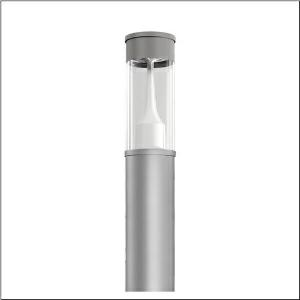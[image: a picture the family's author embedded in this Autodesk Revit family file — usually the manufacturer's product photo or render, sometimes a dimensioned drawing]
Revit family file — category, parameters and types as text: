
# Revit family: city-light_400_iq___st1_2a_5xa5305mf14hp_fa50
name_source: partatom
category: Lighting Fixtures
units: mm (PartAtom-declared; Revit-internal decimal feet)

## family parameters
Cut with Voids When Loaded = No
Host = Face
Light Source = No
Part Type = Normal
Room Calculation Point = No
Round Connector Dimension = Use Diameter
Shared = No

## types (1)
- --- (1 x LED, 4240 lm, 33.6 W, 2700K)
    Apparent Load = 34 VA
    CIE Flux Codes = 22 61 94 96 100
    Color Rendering = 70
    Color Temperature = 2700K
    Default Elevation = 1800 mm
    Description = City-Light 400 iQ, light pillar, Module 540 iQ-SR, primary light control with 3 zone facetted reflector, of plastic, silver coated, highly specular, structured, primary optical cover: cover, of PMMA, transparent, partly coated, light distribution: ST1.2a, primary light characteristic: asymmetric, LED, High Power LED, rated luminous flux: 4.240lm, luminous efficacy: 126lm/W, light colour: 727, colour temperature: 2700K, control gear: ECG iQ, control: presetting dimming logarithmic, Street-Remote, Auto-Match, Temp-Guard, Lumen-Switch, Night-Set, Smart-Wire, Light-Fading, Desk-Remote (wireless, voltage-free reading and setting of iQ features in the workshop via application-optimized NFC function/RFID function), optimised constant luminous flux control (CLO 2.0), with terminal, 6-pole, max. 2.5mm², mains connection: 230..240V, AC, 50/60Hz, start of lifetime: 34W, end of service life: 36W, reduction: 15W, luminaire housing, cylindrical, of extruded aluminium section, coated, Siteco® metallic grey (DB 702S), length: 4.694mm, diameter: 200mm, Module 540 iQ-SR, traffic white (RAL 9016), equipment: Power, protection rating (complete): IP65, insulation class (complete): insulation class II (safety insulation), certification: CE, ENEC, VDE, packaging unit: 1 piece

Light Distribution: ST1.2a
    Height = 500 mm
    Lamp = 1 x LED
    Lamp Light Flux = 4240 lm
    Lamp Power = 33.6 W
    Lamp count = 1
    Length = 200 mm  [stored 0.656168 ft]
    Luminous efficacy = 126 lm/W
    Manufacturer = Siteco
    ModVariant = No
    Model = 5XA5305MF14HP
    Mounting Place = Floor
    Mounting Type = Freestanding
    Number of Poles = 1
    OnlyDefault = Yes
    Power Factor = 1
    Product Name = City-Light 400 iQ | ST1.2a
    Product group = light pillar
    ProductGroupID = 1303
    Protection Class = Protection class II
    Protection Degree = IP 65
    RLX_Detail_Level = 1
    RLX_Emergency_Light_Flux = 0 lm
    RLX_Emergency_Type = 0
    RLX_Emergency_Type_DB = No
    RlxData = <blob elided: 53541 chars, md5=7c3e8d45>
    Socket = socket
    Standby Power = 0 W
    System Light Flux = 4240 lm
    System Power = 34 W
    Type Comments = factory setting: luminous flux: 100 % | dim-lin: 254 | 695 mA
    Type Image = l_1006916.jpg
    URL = http://relux.com
    VarID = @adj_084807
    Voltage = 0 V
    Weight = 0.00 kg
    Width = 0 mm  [stored 0 ft]

note: [stored X ft] marks values corroborated as IEEE doubles in the binary element streams (Revit-internal decimal feet)

## geometry (parser evidence)
native form markers: Blend x4, Sweep x11
no freeform markers — native parametric forms only
